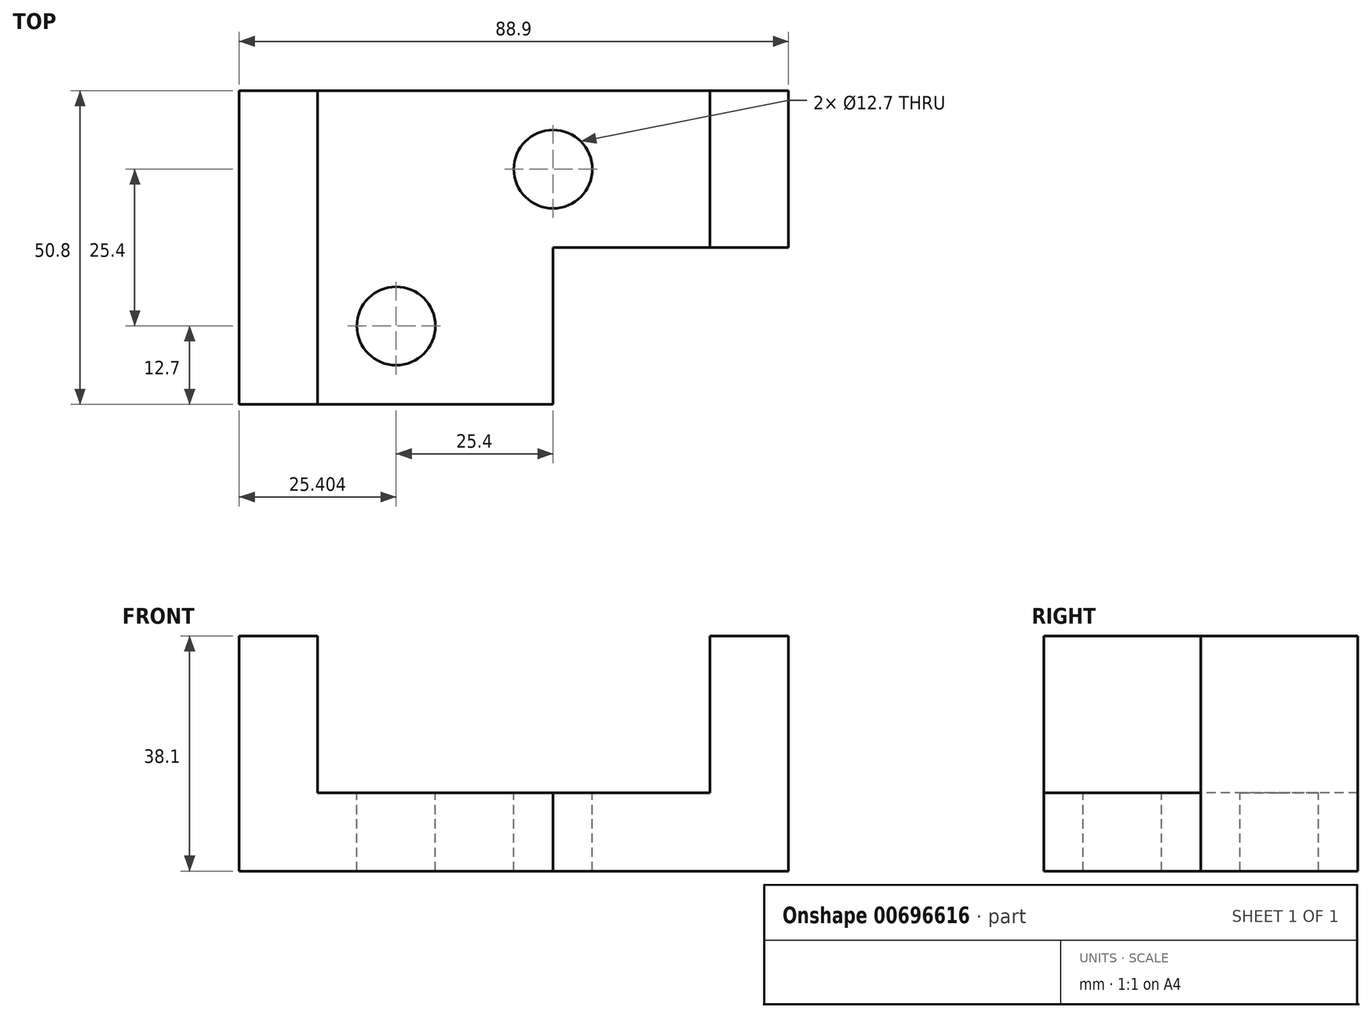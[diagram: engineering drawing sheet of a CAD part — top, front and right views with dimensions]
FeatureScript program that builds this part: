
annotation { "Feature Type Name" : "Feature", "Feature Type Description" : "" }
export const myFeature = defineFeature(function(context is Context, id is Id, definition is map)
    precondition{}
    {
        {
            var Q0;
            Q0=qCreatedBy(makeId("Front.planeOp"),FACE);
            var sketch = newSketch(context, id + "F0", { "sketchPlane" : qUnion([Q0])});
            skLineSegment(sketch, "E0.bottom", {"start": v(34.45, -22.79) * mm, "end": v(-54.45, -22.79) * mm});
            skLineSegment(sketch, "E0.top", {"start": v(34.45, 15.31) * mm, "end": v(-54.45, 15.31) * mm});
            skLineSegment(sketch, "E0.left", {"start": v(34.45, -22.79) * mm, "end": v(34.45, 15.31) * mm});
            skLineSegment(sketch, "E0.right", {"start": v(-54.45, -22.79) * mm, "end": v(-54.45, 15.31) * mm});
            skPoint(sketch, "E0.middle", {"position": v(-10, -3.74) * mm});
            skSolve(sketch);
        }
        {
            var Q0;
            Q0 = qSketchRegion(id + "F0", true);
            extrude(context, id + "F1", {"entities" : qUnion([Q0]), "depth" : 50.8 * mm, "offsetDistance" : 25.4 * mm});
        }
        {
            var Q0;
            Q0=makeQuery(id+"F1.opExtrude","CAP_FACE",FACE,{"disambiguationData":[OSD([sQuery(id+"F0.wireOp",EDGE,"E0.bottom"),sQuery(id+"F0.wireOp",EDGE,"E0.top"),sQuery(id+"F0.wireOp",EDGE,"E0.left"),sQuery(id+"F0.wireOp",EDGE,"E0.right")])],"isStart":false});
            var sketch = newSketch(context, id + "F2", { "sketchPlane" : qUnion([Q0])});
            skLineSegment(sketch, "E1.bottom", {"start": v(-41.75, 15.31) * mm, "end": v(21.75, 15.31) * mm});
            skLineSegment(sketch, "E1.top", {"start": v(-41.75, -10.09) * mm, "end": v(21.75, -10.09) * mm});
            skLineSegment(sketch, "E1.left", {"start": v(-41.75, 15.31) * mm, "end": v(-41.75, -10.09) * mm});
            skLineSegment(sketch, "E1.right", {"start": v(21.75, 15.31) * mm, "end": v(21.75, -10.09) * mm});
            skSolve(sketch);
        }
        {
            var Q0;
            Q0 = qSketchRegion(id + "F2", true);
            extrude(context, id + "F3", {"entities" : qUnion([Q0]), "operationType" : NewBodyOperationType.REMOVE, "endBound" : BoundingType.THROUGH_ALL, "oppositeDirection" : true, "depth" : 51.3 * mm, "offsetDistance" : 25.4 * mm});
        }
        {
            var Q0;
            Q0=makeQuery(id+"F1.opExtrude","SWEPT_FACE",FACE,{"disambiguationData":[OSD([sQuery(id+"F0.wireOp",EDGE,"E0.left")])]});
            var sketch = newSketch(context, id + "F4", { "sketchPlane" : qUnion([Q0])});
            skLineSegment(sketch, "E2.bottom", {"start": v(-50.8, 15.31) * mm, "end": v(-25.4, 15.31) * mm});
            skLineSegment(sketch, "E2.top", {"start": v(-50.8, -22.79) * mm, "end": v(-25.4, -22.79) * mm});
            skLineSegment(sketch, "E2.left", {"start": v(-50.8, 15.31) * mm, "end": v(-50.8, -22.79) * mm});
            skLineSegment(sketch, "E2.right", {"start": v(-25.4, 15.31) * mm, "end": v(-25.4, -22.79) * mm});
            skSolve(sketch);
        }
        {
            var Q0;
            Q0 = qSketchRegion(id + "F4", true);
            extrude(context, id + "F5", {"entities" : qUnion([Q0]), "operationType" : NewBodyOperationType.REMOVE, "oppositeDirection" : true, "depth" : 38.1 * mm, "offsetDistance" : 25.4 * mm});
        }
        {
            var Q0;
            Q0=makeQuery(id+"F3.boolean.opBoolean","COPY",FACE,{"derivedFrom":makeQuery(id+"F3.opExtrude","SWEPT_FACE",FACE,{"disambiguationData":[OSD([sQuery(id+"F2.wireOp",EDGE,"E1.top")])]})});
            var sketch = newSketch(context, id + "F6", { "sketchPlane" : qUnion([Q0])});
            skCircle(sketch, "E3", {"center": v(-29.05, -38.1) * mm, "radius": 6.35 * mm});
            skCircle(sketch, "E4", {"center": v(-3.65, -12.7) * mm, "radius": 6.35 * mm});
            skSolve(sketch);
        }
        {
            var Q0;
            Q0 = qSketchRegion(id + "F6", true);
            extrude(context, id + "F7", {"entities" : qUnion([Q0]), "operationType" : NewBodyOperationType.REMOVE, "endBound" : BoundingType.THROUGH_ALL, "oppositeDirection" : true, "depth" : 25.4 * mm, "offsetDistance" : 25.4 * mm});
        }
    });
